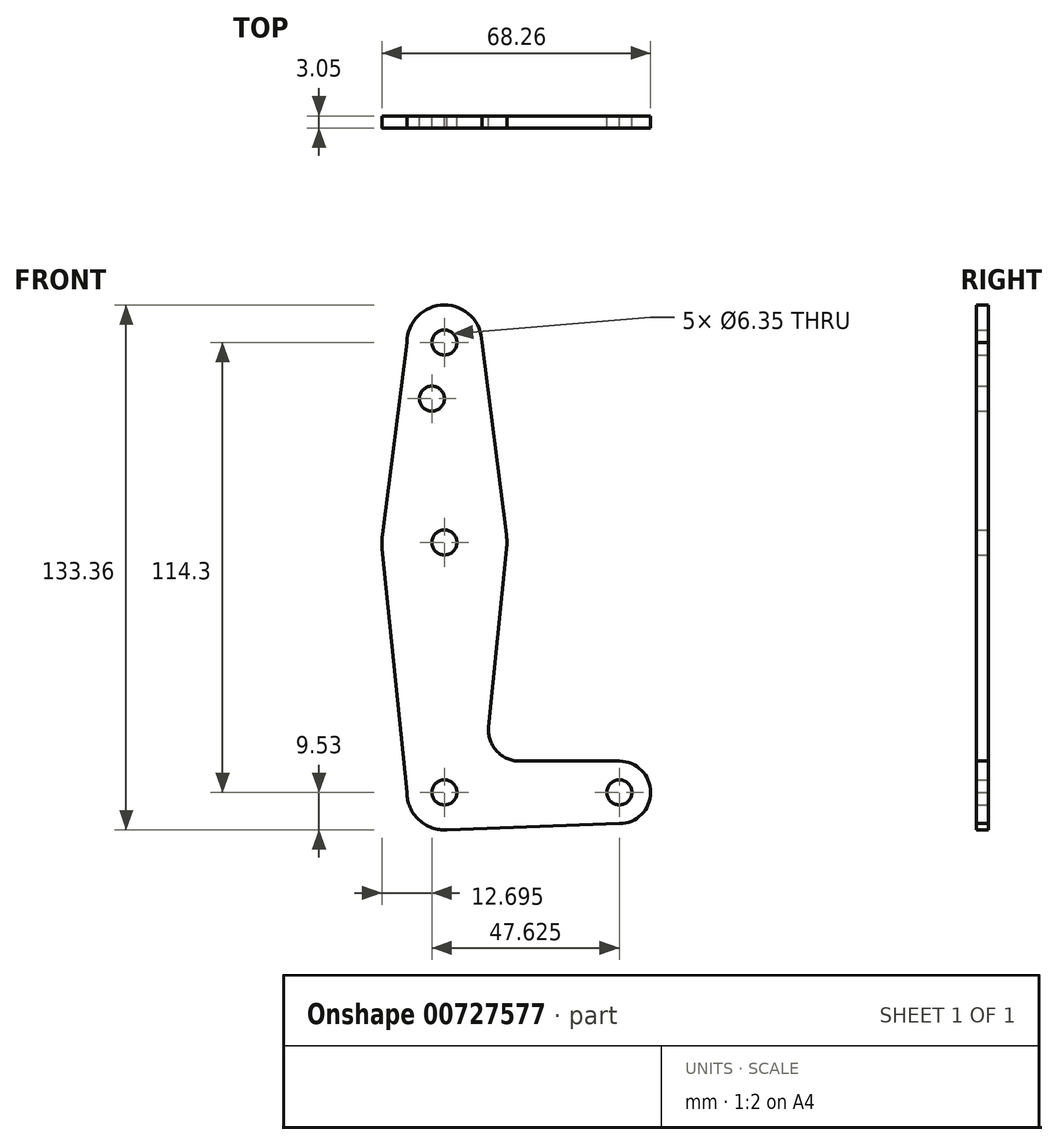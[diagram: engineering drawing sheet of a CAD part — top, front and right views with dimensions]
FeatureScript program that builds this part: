
annotation { "Feature Type Name" : "Feature", "Feature Type Description" : "" }
export const myFeature = defineFeature(function(context is Context, id is Id, definition is map)
    precondition{}
    {
        {
            var Q0;
            Q0=qCreatedBy(makeId("Front.planeOp"),FACE);
            var sketch = newSketch(context, id + "F0", { "sketchPlane" : qUnion([Q0])});
            skLineSegment(sketch, "E0", {"start": v(0, 114.3) * mm, "end": v(0, 0) * mm});
            skLineSegment(sketch, "E1", {"start": v(0, 0) * mm, "end": v(44.45, 0) * mm});
            skCircle(sketch, "E2", {"center": v(0, 114.3) * mm, "radius": 9.53 * mm});
            skCircle(sketch, "E3", {"center": v(0, 63.5) * mm, "radius": 15.88 * mm});
            skCircle(sketch, "E4", {"center": v(0, 0) * mm, "radius": 9.53 * mm});
            skCircle(sketch, "E5", {"center": v(44.45, 0) * mm, "radius": 7.94 * mm});
            skCircle(sketch, "E6", {"center": v(0, 114.3) * mm, "radius": 3.18 * mm});
            skCircle(sketch, "E7", {"center": v(0, 63.5) * mm, "radius": 1.59 * mm});
            skLineSegment(sketch, "E8", {"start": v(0, -9.52) * mm, "end": v(44.45, -7.94) * mm});
            skLineSegment(sketch, "E9", {"start": v(19.12, 7.94) * mm, "end": v(44.45, 7.94) * mm});
            skArc(sketch, "E10.filletArc", {"start": v(11.22, 16.69) * mm, "mid": v(13.23, 10.56) * mm, "end": v(19.12, 7.94) * mm});
            skCircle(sketch, "E11", {"center": v(-3.18, 100.03) * mm, "radius": 3.18 * mm});
            skCircle(sketch, "E12", {"center": v(0, 0) * mm, "radius": 3.18 * mm});
            skCircle(sketch, "E13", {"center": v(44.45, 0) * mm, "radius": 3.18 * mm});
            skCircle(sketch, "E14", {"center": v(0, 63.5) * mm, "radius": 3.18 * mm});
            skLineSegment(sketch, "E15", {"start": v(-15.75, 65.5) * mm, "end": v(-9.53, 114.3) * mm});
            skLineSegment(sketch, "E16", {"start": v(-9.53, 0) * mm, "end": v(-15.8, 61.9) * mm});
            skLineSegment(sketch, "E17", {"start": v(9.52, 114.3) * mm, "end": v(15.75, 65.5) * mm});
            skLineSegment(sketch, "E18", {"start": v(15.8, 61.9) * mm, "end": v(11.22, 16.69) * mm});
            skSolve(sketch);
        }
        {
            var Q0;
            Q0 = qSketchRegion(id + "F0", true);
            var Q1;
            {var subQ0=sQuery(id+"F0.wireOp",EDGE,"E4");var subQ1=sQuery(id+"F0.wireOp",EDGE,"E0");var subQ2=makeQuery(id+"F0.imprint","INTERSECT",VERTEX,{"derivedFrom":[subQ1,subQ0]});Q1=makeQuery(id+"F0.imprint","IMPRINT",FACE,{"disambiguationData":[TD([[makeQuery(id+"F0.imprint","IMPRINT",EDGE,{"disambiguationData":[TD([[subQ2,-1.0]])],"derivedFrom":subQ1}),1.0]])]});}
            extrude(context, id + "F1", {"entities" : qUnion([Q0, Q1]), "depth" : 3.05 * mm, "offsetDistance" : 25.4 * mm});
        }
    });
